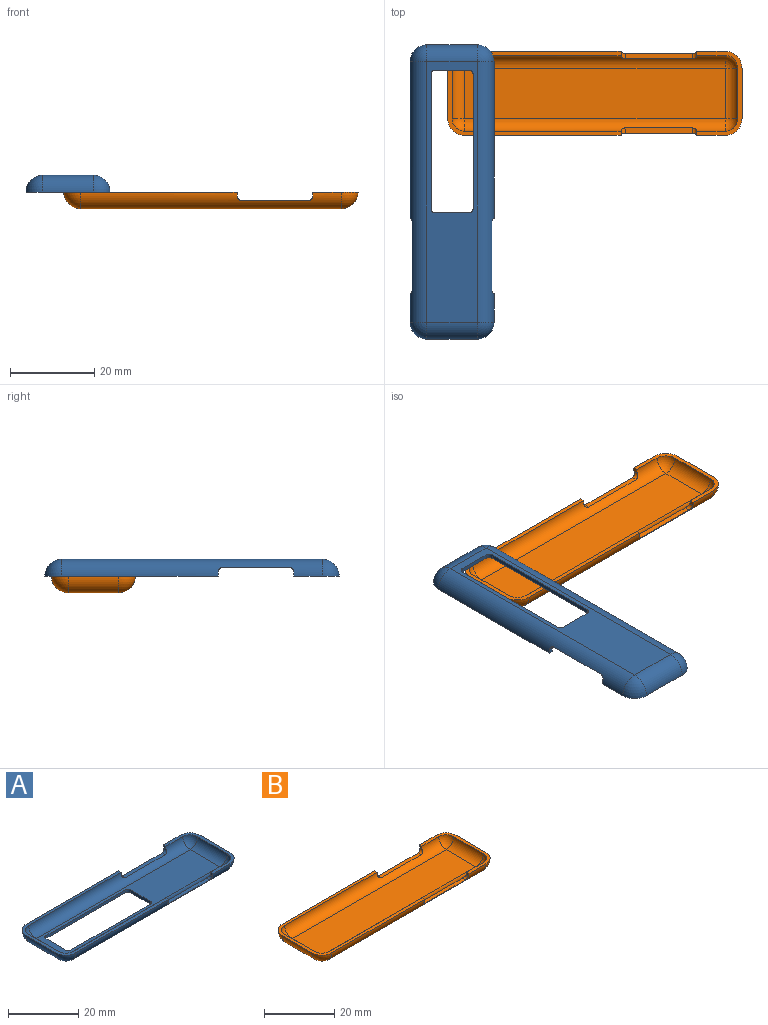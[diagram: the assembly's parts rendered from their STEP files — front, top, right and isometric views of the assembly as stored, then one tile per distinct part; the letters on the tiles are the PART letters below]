
ASSEMBLY  parts=2 mates=1
PART A: 38 faces, bbox 70x20x4 mm
  f0: plane 62x12mm, normal (0,0,-1), area 404.9mm2, adj f5,f6,f9,f10,f30,f31,f32,f33
  f1: plane 62x12mm, normal (0,0,1), area 404.9mm2, adj f13,f14,f17,f18,f30,f31,f32,f33
  f2: plane 41.21x20mm, normal (0,0,1), area 97.4mm2, adj f4,f5,f6,f8,f10,f12,f13,f14
  f3: plane 20x10.81mm, normal (0,0,1), area 36.6mm2, adj f5,f7,f9,f10,f11,f13,f15,f17
  f4: sphere r=4mm, area 25.1mm2, adj f2,f5,f6
  f5: cylinder r=4mm len=62mm, axis (-1,0,0), area 352.4mm2, adj f0,f2,f3,f4,f7,f23,f24,f25
  f6: cylinder r=4mm len=12mm, axis (0,-1,0), area 75.4mm2, adj f0,f2,f4,f8
  f7: sphere r=4mm, area 25.1mm2, adj f3,f5,f9
  f8: sphere r=4mm, area 25.1mm2, adj f2,f6,f10
  f9: cylinder r=4mm len=12mm, axis (0,1,0), area 75.4mm2, adj f0,f3,f7,f11
  f10: cylinder r=4mm len=62mm, axis (1,0,0), area 352.4mm2, adj f0,f2,f3,f8,f11,f20,f21,f22
  f11: sphere r=4mm, area 25.1mm2, adj f3,f9,f10
  f12: sphere r=3mm, area 14.1mm2, adj f2,f13,f14
  f13: cylinder r=3mm len=62mm, axis (-1,0,0), area 253.3mm2, adj f1,f2,f3,f12,f15,f23,f24,f25
  f14: cylinder r=3mm len=12mm, axis (0,-1,0), area 56.5mm2, adj f1,f2,f12,f16
  f15: sphere r=3mm, area 14.1mm2, adj f3,f13,f17
  f16: sphere r=3mm, area 14.1mm2, adj f2,f14,f18
  f17: cylinder r=3mm len=12mm, axis (0,1,0), area 56.5mm2, adj f1,f3,f15,f19
  f18: cylinder r=3mm len=62mm, axis (1,0,0), area 253.3mm2, adj f1,f2,f3,f16,f19,f20,f21,f22
  f19: sphere r=3mm, area 14.1mm2, adj f3,f17,f18
  f20: plane 15.98x1.23mm, normal (0,0,1), area 19.6mm2, adj f10,f18,f28,f29
  f21: plane 1.17x1mm, normal (1,0,0), area 1mm2, adj f2,f10,f18,f28
  f22: plane 1.17x1mm, normal (-1,0,0), area 1mm2, adj f3,f10,f18,f29
  f23: plane 1.17x1mm, normal (-1,0,0), area 1mm2, adj f3,f5,f13,f26
  f24: plane 1.17x1mm, normal (1,0,0), area 1mm2, adj f2,f5,f13,f27
  f25: plane 15.98x1.23mm, normal (0,0,1), area 19.6mm2, adj f5,f13,f26,f27
  f26: cylinder r=1mm len=1.64mm, axis (0,1,0), area 1.8mm2, adj f5,f13,f23,f25
  f27: cylinder r=1mm len=1.64mm, axis (0,-1,0), area 1.8mm2, adj f5,f13,f24,f25
  f28: cylinder r=1mm len=1.64mm, axis (0,-1,0), area 1.8mm2, adj f10,f18,f20,f21
  f29: cylinder r=1mm len=1.64mm, axis (0,1,0), area 1.8mm2, adj f10,f18,f20,f22
  f30: plane 8x1mm, normal (-1,0,0), area 8mm2, adj f0,f1,f34,f35
  f31: plane 32x1mm, normal (0,-1,0), area 32mm2, adj f0,f1,f34,f36
  f32: plane 32x1mm, normal (0,1,0), area 32mm2, adj f0,f1,f35,f37
  f33: plane 8x1mm, normal (1,0,0), area 8mm2, adj f0,f1,f36,f37
  f34: cylinder r=1mm len=1mm, axis (0,0,1), area 1.6mm2, adj f0,f1,f30,f31
  f35: cylinder r=1mm len=1mm, axis (0,0,-1), area 1.6mm2, adj f0,f1,f30,f32
  f36: cylinder r=1mm len=1mm, axis (0,0,-1), area 1.6mm2, adj f0,f1,f31,f33
  f37: cylinder r=1mm len=1mm, axis (0,0,1), area 1.6mm2, adj f0,f1,f32,f33
PART B: 30 faces, bbox 70x20x4 mm
  f0: plane 41.21x20mm, normal (0,0,1), area 97.4mm2, adj f3,f4,f5,f7,f9,f12,f13,f14
  f1: plane 20x10.81mm, normal (0,0,1), area 36.6mm2, adj f4,f6,f8,f9,f10,f13,f15,f17
  f2: plane 62x12mm, normal (0,0,-1), area 744mm2, adj f4,f5,f8,f9
  f3: sphere r=4mm, area 25.1mm2, adj f0,f4,f5
  f4: cylinder r=4mm len=62mm, axis (-1,0,0), area 352.4mm2, adj f0,f1,f2,f3,f6,f23,f24,f25
  f5: cylinder r=4mm len=12mm, axis (0,-1,0), area 75.4mm2, adj f0,f2,f3,f7
  f6: sphere r=4mm, area 25.1mm2, adj f1,f4,f8
  f7: sphere r=4mm, area 25.1mm2, adj f0,f5,f9
  f8: cylinder r=4mm len=12mm, axis (0,1,0), area 75.4mm2, adj f1,f2,f6,f10
  f9: cylinder r=4mm len=62mm, axis (1,0,0), area 352.4mm2, adj f0,f1,f2,f7,f10,f20,f21,f22
  f10: sphere r=4mm, area 25.1mm2, adj f1,f8,f9
  f11: plane 62x12mm, normal (0,0,1), area 744mm2, adj f13,f14,f17,f18
  f12: sphere r=3mm, area 14.1mm2, adj f0,f13,f14
  f13: cylinder r=3mm len=62mm, axis (-1,0,0), area 253.3mm2, adj f0,f1,f11,f12,f15,f23,f24,f25
  f14: cylinder r=3mm len=12mm, axis (0,-1,0), area 56.5mm2, adj f0,f11,f12,f16
  f15: sphere r=3mm, area 14.1mm2, adj f1,f13,f17
  f16: sphere r=3mm, area 14.1mm2, adj f0,f14,f18
  f17: cylinder r=3mm len=12mm, axis (0,1,0), area 56.5mm2, adj f1,f11,f15,f19
  f18: cylinder r=3mm len=62mm, axis (1,0,0), area 253.3mm2, adj f0,f1,f11,f16,f19,f20,f21,f22
  f19: sphere r=3mm, area 14.1mm2, adj f1,f17,f18
  f20: plane 15.98x1.23mm, normal (0,0,1), area 19.6mm2, adj f9,f18,f28,f29
  f21: plane 1.17x1mm, normal (1,0,0), area 1mm2, adj f0,f9,f18,f28
  f22: plane 1.17x1mm, normal (-1,0,0), area 1mm2, adj f1,f9,f18,f29
  f23: plane 1.17x1mm, normal (-1,0,0), area 1mm2, adj f1,f4,f13,f26
  f24: plane 1.17x1mm, normal (1,0,0), area 1mm2, adj f0,f4,f13,f27
  f25: plane 15.98x1.23mm, normal (0,0,1), area 19.6mm2, adj f4,f13,f26,f27
  f26: cylinder r=1mm len=1.64mm, axis (0,1,0), area 1.8mm2, adj f4,f13,f23,f25
  f27: cylinder r=1mm len=1.64mm, axis (0,-1,0), area 1.8mm2, adj f4,f13,f24,f25
  f28: cylinder r=1mm len=1.64mm, axis (0,-1,0), area 1.8mm2, adj f9,f18,f20,f21
  f29: cylinder r=1mm len=1.64mm, axis (0,1,0), area 1.8mm2, adj f9,f18,f20,f22
PLACE A rot(axis=(0.71,-0.71,0),180deg) t=(-34,-23.47,8)mm
PLACE B at identity
MATE parallel A.f2 <-> B.f0  axis (0,0,-1) through (-34,-6,4)mm
